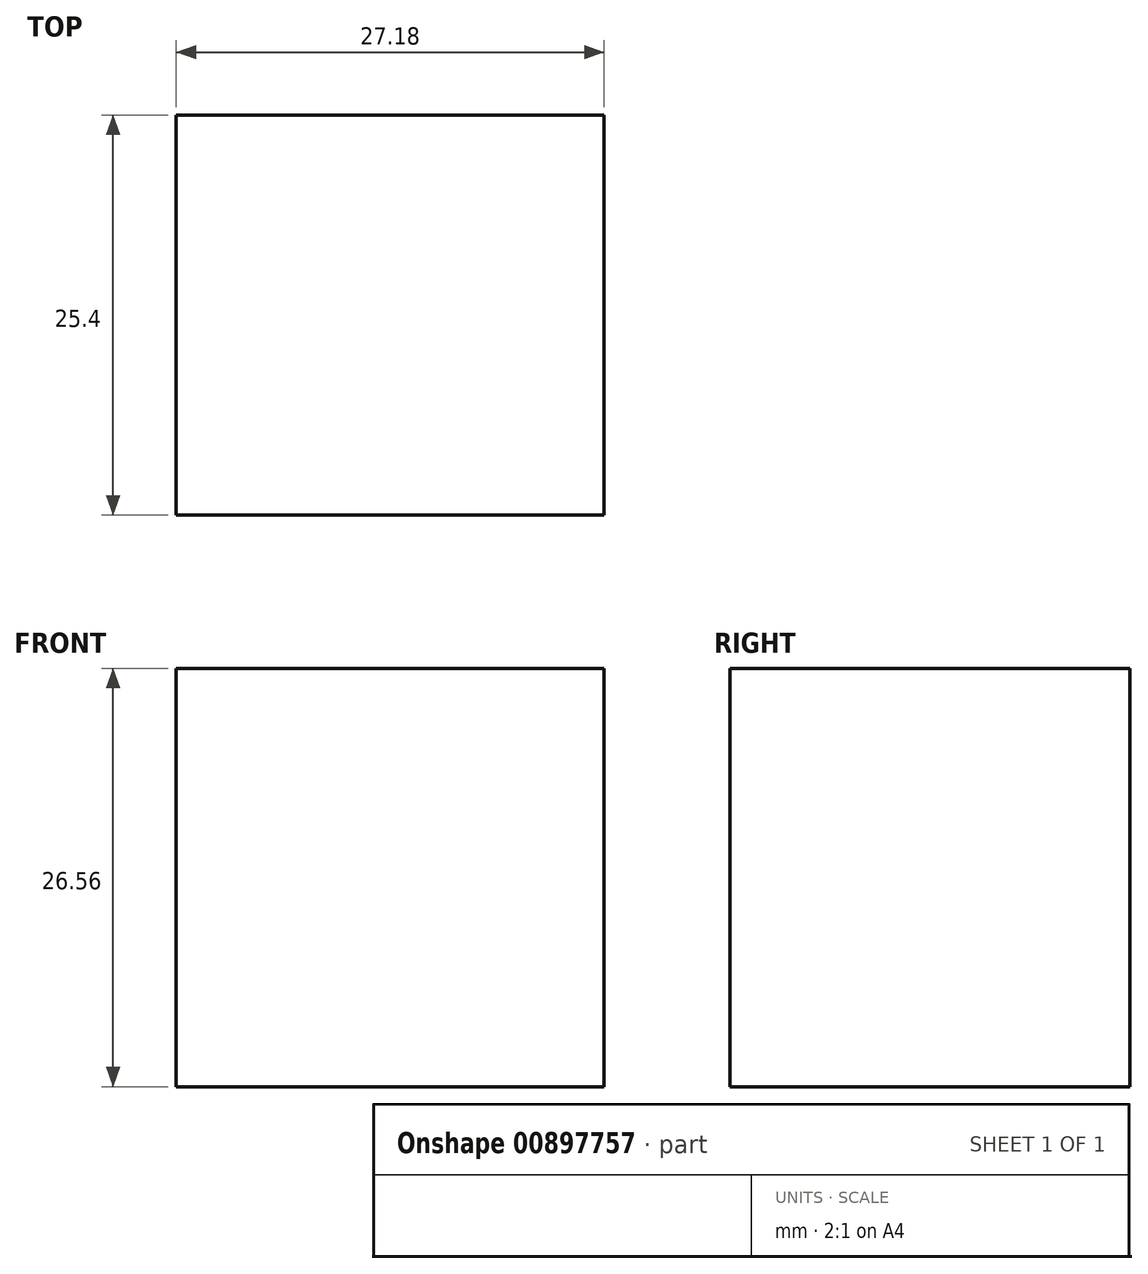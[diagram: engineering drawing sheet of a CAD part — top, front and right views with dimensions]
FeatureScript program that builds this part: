
annotation { "Feature Type Name" : "Feature", "Feature Type Description" : "" }
export const myFeature = defineFeature(function(context is Context, id is Id, definition is map)
    precondition{}
    {
        {
            var Q0;
            Q0=qCreatedBy(makeId("Front.planeOp"),FACE);
            var sketch = newSketch(context, id + "F0", { "sketchPlane" : qUnion([Q0])});
            skLineSegment(sketch, "E0.bottom", {"start": v(13.59, -13.28) * mm, "end": v(-13.59, -13.28) * mm});
            skLineSegment(sketch, "E0.top", {"start": v(13.59, 13.28) * mm, "end": v(-13.59, 13.28) * mm});
            skLineSegment(sketch, "E0.left", {"start": v(13.59, -13.28) * mm, "end": v(13.59, 13.28) * mm});
            skLineSegment(sketch, "E0.right", {"start": v(-13.59, -13.28) * mm, "end": v(-13.59, 13.28) * mm});
            skPoint(sketch, "E0.middle", {"position": v(0, 0) * mm});
            skSolve(sketch);
        }
        {
            var Q0;
            Q0 = qSketchRegion(id + "F0", true);
            extrude(context, id + "F1", {"entities" : qUnion([Q0]), "depth" : 25.4 * mm, "offsetDistance" : 25.4 * mm});
        }
    });
